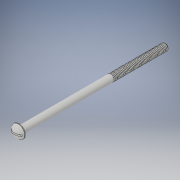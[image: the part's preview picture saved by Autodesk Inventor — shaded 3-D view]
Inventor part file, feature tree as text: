
AUTODESK INVENTOR PART (.ipt)
format: ipt  version: 2018 (Build 220112000, 112)  size: 1,095,168 bytes
history: native  units: in
note: dims shown in document units (in); Inventor stores cm internally (conversion verified against a paired STEP export)
features: other x1, extrude x1
ambient origin geometry x8: Origin, YZ Plane, XZ Plane, XY Plane, X Axis, Y Axis, Z Axis, Center Point
bodies: Solid1 (feature_tree)
feature tree (2):
  other  "91783A846_18-8 SS ROUND HEAD SLOTTED MACHINE SCREW1"
  extrude  "Extrude12"  [1 undecoded]
note: 1 required parameter value undecoded (feature->parameter linkage not recoverable at this tier; creation-order binding heuristic only, values carry confidence <= 0.55)
